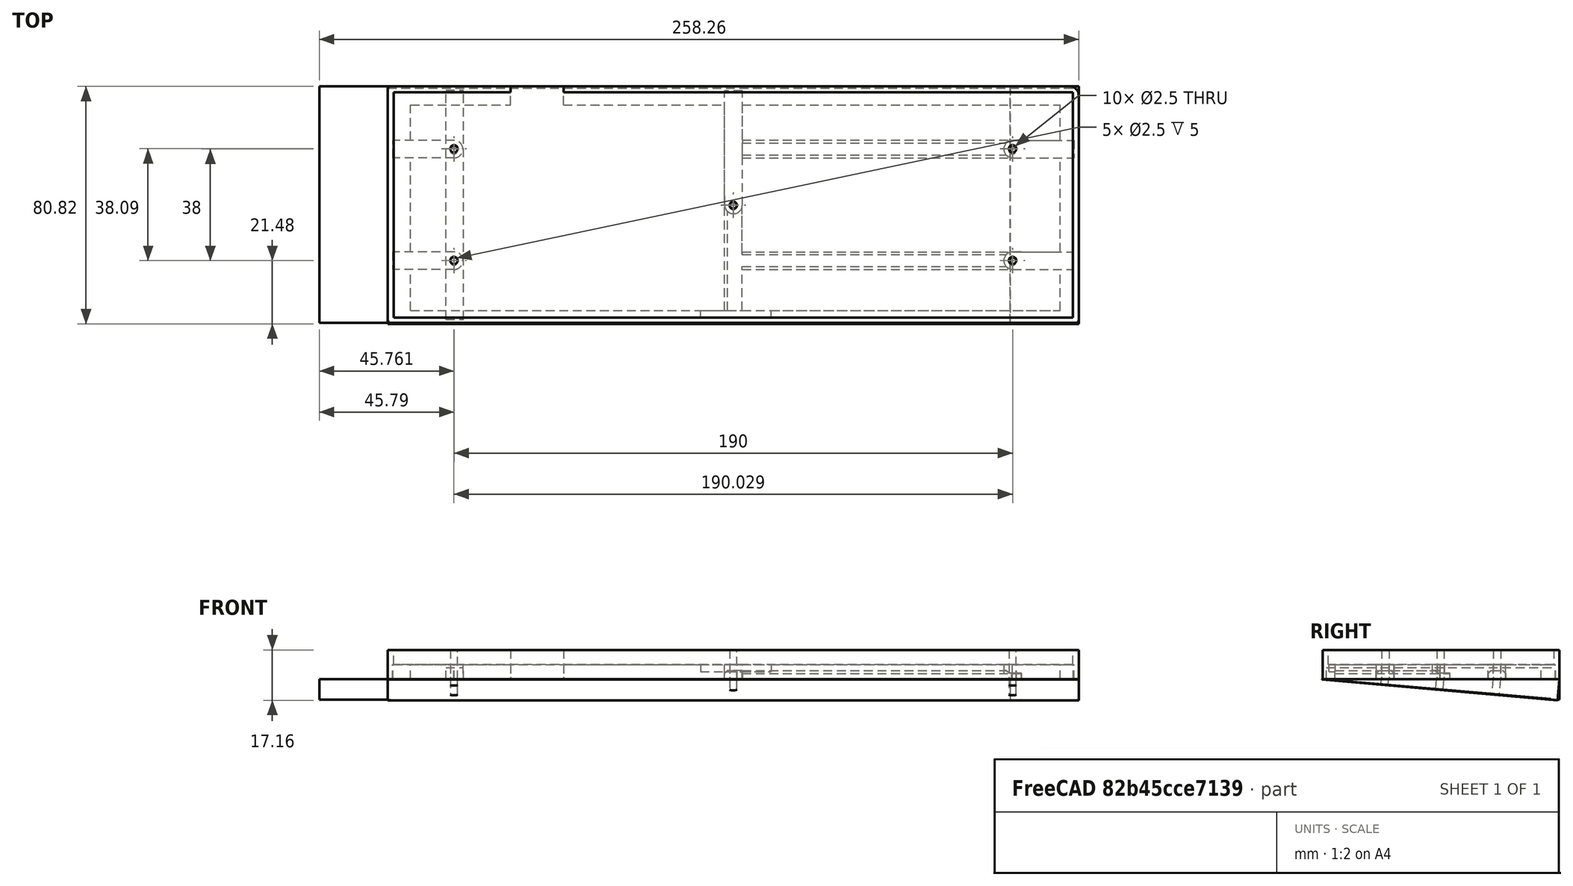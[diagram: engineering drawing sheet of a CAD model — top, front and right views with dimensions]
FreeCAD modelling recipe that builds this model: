
FCSTD DOCUMENT  (FreeCAD 0.19R24291 (Git))
Label: simpleContraCase
License: All rights reserved
LicenseURL: http://en.wikipedia.org/wiki/All_rights_reserved
objects: Sketcher::SketchObject×10, PartDesign::Body×9, PartDesign::Pad×8, Part::Cut×7, Part::Box×7, Part::MultiFuse×5, Part::FeaturePython×4, Part::Chamfer×3, Part::Cylinder×2, Part::Fillet×2, Mesh::Feature×1
note: 65 computed .brp shape members not serialized (recipe doc carries the construction recipe); baked Part::Feature solids carry a one-line shape summary decoded from their .brp

FEATURE [Sketcher::SketchObject] Sketch
  FullyConstrained = false
  MapMode = 5
  Support = -> [XY_Plane]
  sketch-geometry (9):
    g0: LineSegment StartX=23.2614 StartY=90.31 StartZ=0 EndX=258.261 EndY=90.31 EndZ=0
    g1: LineSegment StartX=258.261 StartY=90.31 StartZ=0 EndX=258.261 EndY=9.81 EndZ=0
    g2: LineSegment StartX=258.261 StartY=9.81 StartZ=0 EndX=23.2614 EndY=9.81 EndZ=0
    g3: LineSegment StartX=23.2614 StartY=9.81 StartZ=0 EndX=23.2614 EndY=90.31 EndZ=0
    g4: Circle CenterX=140.761 CenterY=49.81 CenterZ=0 NormalX=0 NormalY=0 NormalZ=1 AngleXU=0 Radius=1.25
    g5: Circle CenterX=45.7614 CenterY=31.06 CenterZ=0 NormalX=0 NormalY=0 NormalZ=1 AngleXU=0 Radius=1.25
    g6: Circle CenterX=45.7614 CenterY=69.06 CenterZ=0 NormalX=0 NormalY=0 NormalZ=1 AngleXU=0 Radius=1.25
    g7: Circle CenterX=235.761 CenterY=31.06 CenterZ=0 NormalX=0 NormalY=0 NormalZ=1 AngleXU=0 Radius=1.25
    g8: Circle CenterX=235.761 CenterY=69.06 CenterZ=0 NormalX=0 NormalY=0 NormalZ=1 AngleXU=0 Radius=1.25
  constraints (26):
    c: Coincident(g0,g1)
    c: Coincident(g1,g2)
    c: Coincident(g2,g3)
    c: Coincident(g3,g0)
    c: Horizontal(g0)
    c: Horizontal(g2)
    c: Vertical(g1)
    c: Vertical(g3)
    c: DistanceX(g0,g0) = 235
    c: DistanceY(g1,g1) = 80.5
    c: Radius(g4) = 1.25
    c: DistanceY(g2,g4) = 40
    c: DistanceX(g2,g4) = 117.5
    c: Radius(g5) = 1.25
    c: Equal(g5,g6)
    c: DistanceX(g5,g6) = 0
    c: DistanceY(g5,g6) = 38
    c: DistanceY(g6,g0) = 21.25
    c: Equal(g5,g7) = 1.25
    c: Equal(g7,g8)
    c: DistanceX(g7,g8) = 0
    c: DistanceY(g7,g8) = 38
    c: DistanceY(g6,g8) = 0
    c: DistanceX(g6,g8) = 190
    c: DistanceX(g7,g1) = 22.5
    c: DistanceY(g-1,g2) = 9.81
FEATURE [PartDesign::Pad] Pad
  Direction = (1,1,1)
  Length = 10
  Length2 = 100
  Profile = -> Sketch
  Type = 0
FEATURE [PartDesign::Body] Body
  Group = -> [Sketch,Pad]
  Origin = -> Origin
  Tip = -> Pad
FEATURE [Sketcher::SketchObject] Sketch001  label="pcb"
  FullyConstrained = false
  MapMode = 5
  Support = -> [XY_Plane002]
  sketch-geometry (9):
    g0: LineSegment StartX=25.287 StartY=88.3498 StartZ=0 EndX=256.287 EndY=88.3498 EndZ=0
    g1: LineSegment StartX=256.287 StartY=88.3498 StartZ=0 EndX=256.287 EndY=11.6498 EndZ=0
    g2: LineSegment StartX=256.287 StartY=11.6498 StartZ=0 EndX=25.287 EndY=11.6498 EndZ=0
    g3: LineSegment StartX=25.287 StartY=11.6498 StartZ=0 EndX=25.287 EndY=88.3498 EndZ=0
    g4: Circle CenterX=140.787 CenterY=49.9498 CenterZ=0 NormalX=0 NormalY=0 NormalZ=1 AngleXU=0 Radius=1.25
    g5: Circle CenterX=45.787 CenterY=31.0498 CenterZ=0 NormalX=0 NormalY=0 NormalZ=1 AngleXU=0 Radius=1.25
    g6: Circle CenterX=45.787 CenterY=69.0498 CenterZ=0 NormalX=0 NormalY=0 NormalZ=1 AngleXU=0 Radius=1.25
    g7: Circle CenterX=235.787 CenterY=31.0498 CenterZ=0 NormalX=0 NormalY=0 NormalZ=1 AngleXU=0 Radius=1.25
    g8: Circle CenterX=235.787 CenterY=69.0498 CenterZ=0 NormalX=0 NormalY=0 NormalZ=1 AngleXU=0 Radius=1.25
  constraints (25):
    c: Coincident(g0,g1)
    c: Coincident(g1,g2)
    c: Coincident(g2,g3)
    c: Coincident(g3,g0)
    c: Horizontal(g0)
    c: Horizontal(g2)
    c: Vertical(g1)
    c: Vertical(g3)
    c: DistanceX(g0,g0) = 231
    c: DistanceY(g1,g1) = 76.7
    c: Radius(g4) = 1.25
    c: DistanceY(g2,g4) = 38.3
    c: DistanceX(g2,g4) = 115.5
    c: Radius(g5) = 1.25
    c: Equal(g5,g6)
    c: DistanceX(g5,g6) = 0
    c: DistanceY(g5,g6) = 38
    c: Equal(g5,g7) = 1.25
    c: Equal(g7,g8)
    c: DistanceX(g7,g8) = 0
    c: DistanceY(g7,g8) = 38
    c: DistanceY(g6,g8) = 0
    c: DistanceX(g6,g8) = 190
    c: DistanceX(g7,g1) = 20.5
    c: DistanceY(g8,g0) = 19.3
FEATURE [Sketcher::SketchObject] Sketch002
  FullyConstrained = false
  MapMode = 5
  Support = -> [XY_Plane002]
  sketch-geometry (9):
    g0: LineSegment StartX=25.287 StartY=88.3498 StartZ=0 EndX=256.287 EndY=88.3498 EndZ=0
    g1: LineSegment StartX=256.287 StartY=88.3498 StartZ=0 EndX=256.287 EndY=11.6498 EndZ=0
    g2: LineSegment StartX=256.287 StartY=11.6498 StartZ=0 EndX=25.287 EndY=11.6498 EndZ=0
    g3: LineSegment StartX=25.287 StartY=11.6498 StartZ=0 EndX=25.287 EndY=88.3498 EndZ=0
    g4: Circle CenterX=140.787 CenterY=49.9498 CenterZ=0 NormalX=0 NormalY=0 NormalZ=1 AngleXU=0 Radius=1.25
    g5: Circle CenterX=45.787 CenterY=31.0498 CenterZ=0 NormalX=0 NormalY=0 NormalZ=1 AngleXU=0 Radius=1.25
    g6: Circle CenterX=45.787 CenterY=69.0498 CenterZ=0 NormalX=0 NormalY=0 NormalZ=1 AngleXU=0 Radius=1.25
    g7: Circle CenterX=235.787 CenterY=31.0498 CenterZ=0 NormalX=0 NormalY=0 NormalZ=1 AngleXU=0 Radius=1.25
    g8: Circle CenterX=235.787 CenterY=69.0498 CenterZ=0 NormalX=0 NormalY=0 NormalZ=1 AngleXU=0 Radius=1.25
  constraints (25):
    c: Coincident(g0,g1)
    c: Coincident(g1,g2)
    c: Coincident(g2,g3)
    c: Coincident(g3,g0)
    c: Horizontal(g0)
    c: Horizontal(g2)
    c: Vertical(g1)
    c: Vertical(g3)
    c: DistanceX(g0,g0) = 231
    c: DistanceY(g1,g1) = 76.7
    c: Radius(g4) = 1.25
    c: DistanceY(g2,g4) = 38.3
    c: DistanceX(g2,g4) = 115.5
    c: Radius(g5) = 1.25
    c: Equal(g5,g6)
    c: DistanceX(g5,g6) = 0
    c: DistanceY(g5,g6) = 38
    c: Equal(g5,g7) = 1.25
    c: Equal(g7,g8)
    c: DistanceX(g7,g8) = 0
    c: DistanceY(g7,g8) = 38
    c: DistanceY(g6,g8) = 0
    c: DistanceX(g6,g8) = 190
    c: DistanceX(g7,g1) = 20.5
    c: DistanceY(g8,g0) = 19.3
FEATURE [PartDesign::Pad] Pad001
  Direction = (1,1,1)
  Length = 6
  Length2 = 100
  Profile = -> Sketch002
  Type = 0
FEATURE [PartDesign::Body] Body001
  Group = -> [Pad001]
  Origin = -> Origin001
  Tip = -> Pad001
FEATURE [Part::FeaturePython] Clone  label="Pad002"  # Draft clone (typed FeaturePython)
  AttacherType = Attacher::AttachEngine3D
  Fuse = false
  Objects = -> [Pad001]
  Placement = pos=(0,0,5) rot=(0,0,1;0rad)
  Scale = (1,1,2)
FEATURE [Part::Cut] Cut006
  Base = -> Pad
  Tool = -> Clone
FEATURE [Part::Box] Box001  label="Cubo"
  AttacherType = Attacher::AttachEngine3D
  Height = 10
  Length = 221
  Placement = pos=(31,14,0) rot=(0,0,1;0rad)
  Width = 70
FEATURE [Part::Cut] Cut007
  Base = -> Cut006
  Tool = -> Box001
FEATURE [Sketcher::SketchObject] Sketch003  label="pcb001"
  FullyConstrained = false
  MapMode = 5
  Support = -> [XY_Plane003]
  sketch-geometry (10):
    g0: Circle CenterX=140.787 CenterY=49.9731 CenterZ=0 NormalX=0 NormalY=0 NormalZ=1 AngleXU=0 Radius=1.25
    g1: Circle CenterX=45.787 CenterY=30.9731 CenterZ=0 NormalX=0 NormalY=0 NormalZ=1 AngleXU=0 Radius=1.25
    g2: Circle CenterX=45.787 CenterY=68.9731 CenterZ=0 NormalX=0 NormalY=0 NormalZ=1 AngleXU=0 Radius=1.25
    g3: Circle CenterX=235.787 CenterY=30.9731 CenterZ=0 NormalX=0 NormalY=0 NormalZ=1 AngleXU=0 Radius=1.25
    g4: Circle CenterX=235.787 CenterY=68.9731 CenterZ=0 NormalX=0 NormalY=0 NormalZ=1 AngleXU=0 Radius=1.25
    g5: Circle CenterX=140.787 CenterY=49.9731 CenterZ=0 NormalX=0 NormalY=0 NormalZ=1 AngleXU=0 Radius=3
    g6: Circle CenterX=45.787 CenterY=30.9731 CenterZ=0 NormalX=0 NormalY=0 NormalZ=1 AngleXU=0 Radius=3
    g7: Circle CenterX=235.787 CenterY=30.9731 CenterZ=0 NormalX=0 NormalY=0 NormalZ=1 AngleXU=0 Radius=3
    g8: Circle CenterX=235.787 CenterY=68.9731 CenterZ=0 NormalX=0 NormalY=0 NormalZ=1 AngleXU=0 Radius=3
    g9: Circle CenterX=45.787 CenterY=68.9731 CenterZ=0 NormalX=0 NormalY=0 NormalZ=1 AngleXU=0 Radius=3
  constraints (22):
    c: Radius(g0) = 1.25
    c: Radius(g1) = 1.25
    c: Equal(g1,g2)
    c: DistanceX(g1,g2) = 0
    c: DistanceY(g1,g2) = 38
    c: Equal(g1,g3) = 1.25
    c: Equal(g3,g4)
    c: DistanceX(g3,g4) = 0
    c: DistanceY(g3,g4) = 38
    c: DistanceY(g2,g4) = 0
    c: DistanceX(g2,g4) = 190
    c: Coincident(g5,g0)
    c: Radius(g5) = 3
    c: DistanceY(g3,g0) = 19
    c: DistanceX(g1,g0) = 95
    c: Coincident(g6,g1)
    c: Radius(g6) = 3
    c: Coincident(g7,g3)
    c: Radius(g7) = 3
    c: Coincident(g8,g4)
    c: Radius(g8) = 3
    c: Radius(g9) = 3
FEATURE [Sketcher::SketchObject] Sketch004  label="pcb002"
  FullyConstrained = false
  MapMode = 5
  Support = -> [XY_Plane003]
  sketch-geometry (5):
    g0: Circle CenterX=140.82 CenterY=49.97 CenterZ=0 NormalX=0 NormalY=0 NormalZ=1 AngleXU=0 Radius=1.25
    g1: ArcOfCircle CenterX=140.82 CenterY=49.97 CenterZ=0 NormalX=0 NormalY=0 NormalZ=1 AngleXU=0 Radius=3.01165 StartAngle=3.22247 EndAngle=6.20231
    g2: LineSegment StartX=137.818 StartY=49.7267 StartZ=0 EndX=137.818 EndY=88.8689 EndZ=0
    g3: LineSegment StartX=143.822 StartY=49.7267 StartZ=0 EndX=143.822 EndY=88.8689 EndZ=0
    g4: LineSegment StartX=143.822 StartY=88.8689 StartZ=0 EndX=137.818 EndY=88.8689 EndZ=0
  constraints (12):
    c: Radius(g0) = 1.25
    c: Coincident(g1,g0)
    c: DistanceY(g0) = 49.97
    c: DistanceX(g0) = 140.82
    c: Coincident(g2,g1)
    c: Vertical(g2)
    c: Coincident(g3,g1)
    c: Vertical(g3)
    c: Equal(g2,g3)
    c: Coincident(g4,g3)
    c: Coincident(g4,g2)
    c: Horizontal(g4)
FEATURE [PartDesign::Pad] Pad002  label="Pad003"
  Direction = (1,1,1)
  Length = 5
  Length2 = 100
  Profile = -> Sketch004
  Type = 0
FEATURE [PartDesign::Body] Body002
  Group = -> [Sketch003,Sketch004,Pad002]
  Origin = -> Origin002
  Tip = -> Pad002
FEATURE [Sketcher::SketchObject] Sketch005  label="pcb003"
  FullyConstrained = false
  MapMode = 5
  Support = -> [XY_Plane005]
  sketch-geometry (5):
    g0: Circle CenterX=45.79 CenterY=68.97 CenterZ=0 NormalX=0 NormalY=0 NormalZ=1 AngleXU=0 Radius=1.25
    g1: ArcOfCircle CenterX=45.79 CenterY=68.97 CenterZ=0 NormalX=0 NormalY=0 NormalZ=1 AngleXU=0 Radius=2.99425 StartAngle=4.72598 EndAngle=7.8404
    g2: LineSegment StartX=45.8307 StartY=71.964 StartZ=0 EndX=25.0546 EndY=71.964 EndZ=0
    g3: LineSegment StartX=45.8307 StartY=65.976 StartZ=0 EndX=25.0546 EndY=65.976 EndZ=0
    g4: LineSegment StartX=25.0546 StartY=65.976 StartZ=0 EndX=25.0546 EndY=71.964 EndZ=0
  constraints (11):
    c: Coincident(g1,g0)
    c: Coincident(g2,g1)
    c: Horizontal(g2)
    c: Coincident(g3,g1)
    c: Horizontal(g3)
    c: Equal(g3,g2)
    c: Coincident(g4,g3)
    c: Coincident(g4,g2)
    c: Vertical(g4)
    c: DistanceX(g-1,g0) = 45.79
    c: DistanceY(g-1,g0) = 68.97
FEATURE [PartDesign::Pad] Pad003  label="Pad004"
  Direction = (1,1,1)
  Length = 5
  Length2 = 100
  Profile = -> Sketch005
  Type = 0
FEATURE [PartDesign::Body] Body003
  Group = -> [Sketch005,Pad003]
  Origin = -> Origin003
  Tip = -> Pad003
FEATURE [Sketcher::SketchObject] Sketch006  label="pcb004"
  FullyConstrained = false
  MapMode = 5
  Support = -> [XY_Plane007]
  sketch-geometry (5):
    g0: Circle CenterX=45.79 CenterY=30.97 CenterZ=0 NormalX=0 NormalY=0 NormalZ=1 AngleXU=0 Radius=1.25
    g1: ArcOfCircle CenterX=45.79 CenterY=30.97 CenterZ=0 NormalX=0 NormalY=0 NormalZ=1 AngleXU=0 Radius=3.0007 StartAngle=4.69086 EndAngle=7.87551
    g2: LineSegment StartX=45.7254 StartY=33.97 StartZ=0 EndX=24.858 EndY=33.97 EndZ=0
    g3: LineSegment StartX=45.7254 StartY=27.97 StartZ=0 EndX=24.858 EndY=27.97 EndZ=0
    g4: LineSegment StartX=24.858 StartY=33.97 StartZ=0 EndX=24.858 EndY=27.97 EndZ=0
  constraints (13):
    c: Radius(g0) = 1.25
    c: DistanceX(g-1,g0) = 45.79
    c: DistanceY(g-1,g0) = 30.97
    c: Coincident(g1,g0)
    c: DistanceY(g1,g1) = 6
    c: Coincident(g2,g1)
    c: Horizontal(g2)
    c: Coincident(g3,g1)
    c: Horizontal(g3)
    c: Equal(g3,g2)
    c: Coincident(g4,g2)
    c: Coincident(g4,g3)
    c: Vertical(g4)
FEATURE [PartDesign::Pad] Pad004  label="Pad005"
  Direction = (1,1,1)
  Length = 5
  Length2 = 100
  Profile = -> Sketch006
  Type = 0
FEATURE [PartDesign::Body] Body004
  Group = -> [Sketch006,Pad004]
  Origin = -> Origin004
  Tip = -> Pad004
FEATURE [Sketcher::SketchObject] Sketch007  label="pcb005"
  FullyConstrained = false
  MapMode = 5
  Support = -> [XY_Plane009]
  sketch-geometry (5):
    g0: Circle CenterX=235.79 CenterY=30.97 CenterZ=0 NormalX=0 NormalY=0 NormalZ=1 AngleXU=0 Radius=1.25
    g1: ArcOfCircle CenterX=235.79 CenterY=30.97 CenterZ=0 NormalX=0 NormalY=0 NormalZ=1 AngleXU=0 Radius=2.99927 StartAngle=1.59549 EndAngle=4.6877
    g2: LineSegment StartX=235.716 StartY=33.9684 StartZ=0 EndX=256.389 EndY=33.9684 EndZ=0
    g3: LineSegment StartX=235.716 StartY=27.9716 StartZ=0 EndX=256.389 EndY=27.9716 EndZ=0
    g4: LineSegment StartX=256.389 StartY=33.9684 StartZ=0 EndX=256.389 EndY=27.9716 EndZ=0
  constraints (11):
    c: DistanceY(g0) = 30.97
    c: DistanceX(g0) = 235.79
    c: Coincident(g1,g0)
    c: Coincident(g2,g1)
    c: Horizontal(g2)
    c: Coincident(g3,g1)
    c: Horizontal(g3)
    c: Equal(g3,g2)
    c: Coincident(g4,g2)
    c: Coincident(g4,g3)
    c: Vertical(g4)
FEATURE [PartDesign::Pad] Pad005  label="Pad006"
  Direction = (1,1,1)
  Length = 5
  Length2 = 100
  Profile = -> Sketch007
  Type = 0
FEATURE [PartDesign::Body] Body005
  Group = -> [Sketch007,Pad005]
  Origin = -> Origin005
  Tip = -> Pad005
FEATURE [Sketcher::SketchObject] Sketch008  label="pcb006"
  FullyConstrained = false
  MapMode = 5
  Support = -> [XY_Plane011]
  sketch-geometry (5):
    g0: Circle CenterX=235.79 CenterY=68.97 CenterZ=0 NormalX=0 NormalY=0 NormalZ=1 AngleXU=0 Radius=1.25
    g1: ArcOfCircle CenterX=235.79 CenterY=68.97 CenterZ=0 NormalX=0 NormalY=0 NormalZ=1 AngleXU=0 Radius=3 StartAngle=1.5708 EndAngle=4.71239
    g2: LineSegment StartX=235.79 StartY=71.97 StartZ=0 EndX=256.615 EndY=71.97 EndZ=0
    g3: LineSegment StartX=235.79 StartY=65.97 StartZ=0 EndX=256.615 EndY=65.97 EndZ=0
    g4: LineSegment StartX=256.615 StartY=71.97 StartZ=0 EndX=256.615 EndY=65.97 EndZ=0
  constraints (11):
    c: DistanceX(g0) = 235.79
    c: DistanceY(g0) = 68.97
    c: Coincident(g1,g0)
    c: DistanceY(g1,g1) = 6
    c: Coincident(g2,g1)
    c: Horizontal(g2)
    c: Coincident(g3,g1)
    c: Horizontal(g3)
    c: Coincident(g4,g2)
    c: Coincident(g4,g3)
    c: Vertical(g4)
FEATURE [PartDesign::Pad] Pad006  label="Pad007"
  Direction = (1,1,1)
  Length = 5
  Length2 = 100
  Profile = -> Sketch008
  Type = 0
FEATURE [PartDesign::Body] Body006
  Group = -> [Sketch008,Pad006]
  Origin = -> Origin006
  Tip = -> Pad006
FEATURE [PartDesign::Body] Body007
  Origin = -> Origin007
FEATURE [Part::Box] Box002  label="Cubo001"
  AttacherType = Attacher::AttachEngine3D
  Height = 4
  Length = 6
  Placement = pos=(43,11,0) rot=(0,0,1;0rad)
  Width = 78
FEATURE [Mesh::Feature] Contra_Case_1_  label="Contra_Case(1)"
  Placement = pos=(140,60,0) rot=(0,0,1;0rad)
FEATURE [Part::Box] Box003  label="Cubo002"
  AttacherType = Attacher::AttachEngine3D
  Height = 10
  Length = 18
  Placement = pos=(65,81,0) rot=(0,0,1;0rad)
  Width = 11
FEATURE [Part::Cut] Cut008
  Base = -> Cut007
  Tool = -> Box003
FEATURE [Part::Box] Box004  label="Cube001"
  AttacherType = Attacher::AttachEngine3D
  Height = 3
  Length = 6
  Placement = pos=(137.8,14,0) rot=(0,0,1;0rad)
  Width = 39
FEATURE [Part::Cylinder] Cylinder014
  Angle = 360
  AttacherType = Attacher::AttachEngine3D
  Height = 10
  Placement = pos=(140.7,49.9,0) rot=(0,0,1;0rad)
  Radius = 2
FEATURE [Part::Cut] Cut009
  Base = -> Box004
  Tool = -> Cylinder014
FEATURE [Part::Box] Box005  label="Cube002"
  AttacherType = Attacher::AttachEngine3D
  Height = 7
  Length = 24
  Placement = pos=(129.6,11.9,2.6) rot=(0,0,1;0rad)
  Width = 7
FEATURE [Part::Box] Box006  label="Cube003"
  AttacherType = Attacher::AttachEngine3D
  Height = 3
  Length = 95
  Placement = pos=(143.8,28,0) rot=(0,0,1;0rad)
  Width = 6
FEATURE [Part::Cylinder] Cylinder015
  Angle = 360
  AttacherType = Attacher::AttachEngine3D
  Height = 10
  Placement = pos=(236.3,31,0) rot=(0,0,1;0rad)
  Radius = 2
FEATURE [Part::Cut] Cut011
  Base = -> Box006
  Tool = -> Cylinder015
FEATURE [Part::FeaturePython] Clone001  label="Cut012"  # Draft clone (typed FeaturePython)
  AttacherType = Attacher::AttachEngine3D
  Fuse = false
  Objects = -> [Cut011]
  Placement = pos=(0,38,0) rot=(0,0,1;0rad)
  Scale = (1,1,1)
FEATURE [Part::MultiFuse] Fusion
  Shapes = -> [Pad006,Clone001]
FEATURE [Part::Chamfer] Chamfer
  Base = -> Fusion
  Edges = 2 edges r=1: [Edge16,Edge21]
FEATURE [Part::MultiFuse] Fusion001
  Shapes = -> [Pad005,Cut011]
FEATURE [Part::Chamfer] Chamfer001
  Base = -> Fusion001
  Edges = 2 edges r=1: [Edge16,Edge21]
FEATURE [Part::MultiFuse] Fusion002
  Shapes = -> [Cut009,Pad002]
FEATURE [Part::Chamfer] Chamfer002
  Base = -> Fusion002
  Edges = 1 edges r=1: [Edge33]
FEATURE [Part::Cut] Cut
  Base = -> Cut008
  Tool = -> Box005
FEATURE [Part::FeaturePython] Clone002  label="Pad008"  # Draft clone (typed FeaturePython)
  AttacherType = Attacher::AttachEngine3D
  Fuse = false
  Objects = -> [Pad]
  Placement = pos=(0,0,-62) rot=(0,0,1;0rad)
  Scale = (1,1,1)
FEATURE [Part::Box] Box  label="Cube"
  AttacherType = Attacher::AttachEngine3D
  Height = 10
  Length = 300
  Placement = pos=(0,2.52752,-62.5) rot=(1,0,0;0.087266rad)
  Width = 100
FEATURE [Part::Cut] Cut012  label="Cut013"
  Base = -> Clone002
  Placement = pos=(0,5.12,62.48) rot=(-1,0,0;0.087266rad)
  Tool = -> Box
FEATURE [Sketcher::SketchObject] Sketch009
  FullyConstrained = true
  MapMode = 5
  Placement = pos=(0,0,0) rot=(0.57735,0.57735,0.57735;2.0944rad)
  Support = -> [YZ_Plane008]
  sketch-geometry (3):
    g0: LineSegment StartX=90.31 StartY=0 StartZ=0 EndX=90.31 EndY=-7 EndZ=0
    g1: LineSegment StartX=90.31 StartY=0 StartZ=0 EndX=9.81 EndY=0 EndZ=0
    g2: LineSegment StartX=9.81 StartY=0 StartZ=0 EndX=90.31 EndY=-7 EndZ=0
  constraints (9):
    c: PointOnObject(g0,g-1)
    c: Vertical(g0)
    c: DistanceY(g0,g0) = 7
    c: Coincident(g1,g0)
    c: PointOnObject(g1,g-1)
    c: DistanceX(g1,g1) = 80.5
    c: Coincident(g2,g1)
    c: Coincident(g2,g0)
    c: DistanceX(g-1,g1) = 9.81
FEATURE [PartDesign::Pad] Pad007  label="Pad009"
  Direction = (1,1,1)
  Length = 235
  Length2 = 100
  Placement = pos=(0,0,0) rot=(0.57735,0.57735,0.57735;2.0944rad)
  Profile = -> Sketch009
  Type = 0
FEATURE [PartDesign::Body] Body008
  Group = -> [Sketch009,Pad007]
  Origin = -> Origin008
  Tip = -> Pad007
FEATURE [Part::FeaturePython] Clone003  label="Pad010"  # Draft clone (typed FeaturePython)
  AttacherType = Attacher::AttachEngine3D
  Fuse = false
  Objects = -> [Pad007]
  Placement = pos=(23.26,0,0) rot=(0.57735,0.57735,0.57735;2.0944rad)
  Scale = (1,1,1)
FEATURE [Part::Fillet] Fillet
  Base = -> Cut
  Edges = 4 edges: [Edge4 r=1,Edge30 r=1,Edge31 r=1,Edge32 r=3]
FEATURE [Part::Fillet] Fillet001
  Base = -> Clone003
  Edges = 2 edges: [Edge3 r=1,Edge4 r=3]
FEATURE [Part::MultiFuse] Fusion003
  Shapes = -> [Pad003,Pad004,Fillet,Chamfer002,Chamfer,Chamfer001]
FEATURE [Part::MultiFuse] Fusion004
  Shapes = -> [Fusion003,Fillet001]
